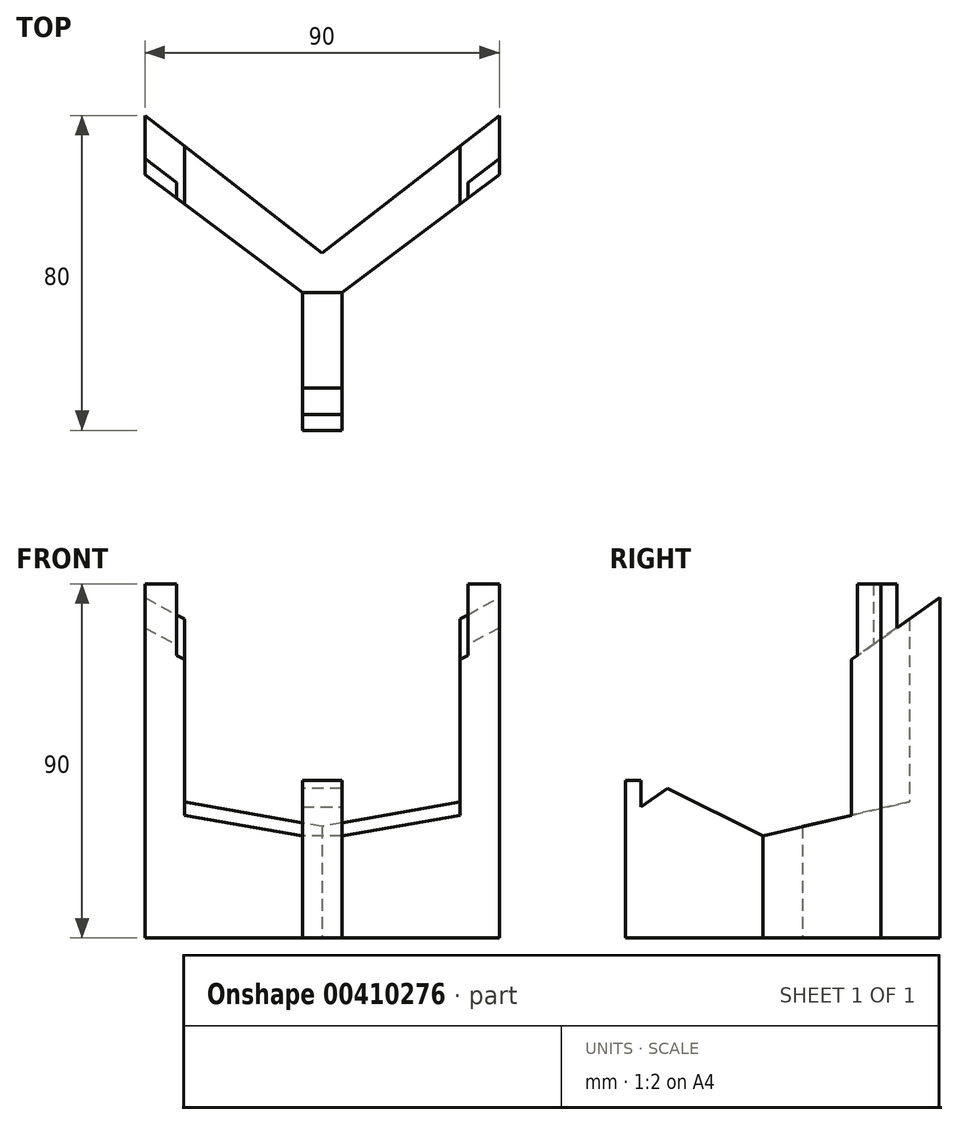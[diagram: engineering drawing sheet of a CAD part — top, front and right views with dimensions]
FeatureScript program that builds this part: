
annotation { "Feature Type Name" : "Feature", "Feature Type Description" : "" }
export const myFeature = defineFeature(function(context is Context, id is Id, definition is map)
    precondition{}
    {
        {
            var Q0;
            Q0=qCreatedBy(makeId("Top.planeOp"),FACE);
            var sketch = newSketch(context, id + "F0", { "sketchPlane" : qUnion([Q0])});
            skLineSegment(sketch, "E0", {"start": v(-5, -35) * mm, "end": v(5, -35) * mm});
            skLineSegment(sketch, "E1", {"start": v(5, -35) * mm, "end": v(5, 0) * mm});
            skLineSegment(sketch, "E2", {"start": v(5, 0) * mm, "end": v(45, 30) * mm});
            skLineSegment(sketch, "E3", {"start": v(45, 30) * mm, "end": v(45, 45) * mm});
            skLineSegment(sketch, "E4", {"start": v(45, 45) * mm, "end": v(0, 10) * mm});
            skLineSegment(sketch, "E5", {"start": v(0, 10) * mm, "end": v(-45, 45) * mm});
            skLineSegment(sketch, "E6", {"start": v(-45, 45) * mm, "end": v(-45, 30) * mm});
            skLineSegment(sketch, "E7", {"start": v(-5, -35) * mm, "end": v(-5, 0) * mm});
            skLineSegment(sketch, "E8", {"start": v(-5, 0) * mm, "end": v(-45, 30) * mm});
            skSolve(sketch);
        }
        {
            var Q0;
            Q0 = qSketchRegion(id + "F0", true);
            extrude(context, id + "F1", {"entities" : qUnion([Q0]), "depth" : 80 * mm});
        }
        {
            var Q0;
            Q0=makeQuery(id+"F1.opExtrude","SWEPT_FACE",FACE,{"disambiguationData":[OSD([sQuery(id+"F0.wireOp",EDGE,"E7")])]});
            var sketch = newSketch(context, id + "F2", { "sketchPlane" : qUnion([Q0])});
            skLineSegment(sketch, "E9", {"start": v(35, 80) * mm, "end": v(-50, 80) * mm});
            skLineSegment(sketch, "E10", {"start": v(-50, 80) * mm, "end": v(35, 20.48) * mm});
            skLineSegment(sketch, "E11", {"start": v(35, 20.48) * mm, "end": v(35, 80) * mm});
            skSolve(sketch);
        }
        {
            var Q0;
            Q0 = qSketchRegion(id + "F2", true);
            extrude(context, id + "F3", {"entities" : qUnion([Q0]), "operationType" : NewBodyOperationType.REMOVE, "endBound" : BoundingType.THROUGH_ALL, "oppositeDirection" : true, "depth" : 25 * mm, "hasSecondDirection" : true, "secondDirectionBound" : SecondDirectionBoundingType.THROUGH_ALL, "secondDirectionOppositeDirection" : false, "secondDirectionDepth" : 25 * mm});
        }
        {
            var Q0;
            Q0=makeQuery(id+"F1.opExtrude","SWEPT_FACE",FACE,{"disambiguationData":[OSD([sQuery(id+"F0.wireOp",EDGE,"E7")])]});
            var sketch = newSketch(context, id + "F4", { "sketchPlane" : qUnion([Q0])});
            skLineSegment(sketch, "E12", {"start": v(24.26, 28) * mm, "end": v(0, 16) * mm});
            skLineSegment(sketch, "E13", {"start": v(0, 16) * mm, "end": v(-51.74, 28) * mm});
            skLineSegment(sketch, "E14", {"start": v(-51.74, 28) * mm, "end": v(-51.74, 88) * mm});
            skLineSegment(sketch, "E15", {"start": v(-51.74, 88) * mm, "end": v(24.26, 88) * mm});
            skLineSegment(sketch, "E16", {"start": v(24.26, 88) * mm, "end": v(24.26, 28) * mm});
            skSolve(sketch);
        }
        {
            var Q0;
            Q0 = qSketchRegion(id + "F4", true);
            extrude(context, id + "F5", {"entities" : qUnion([Q0]), "operationType" : NewBodyOperationType.REMOVE, "oppositeDirection" : true, "depth" : 40 * mm, "hasSecondDirection" : true, "secondDirectionOppositeDirection" : false, "secondDirectionDepth" : 30 * mm});
        }
        {
            var Q0;
            Q0=makeQuery(id+"F1.opExtrude","CAP_FACE",FACE,{"disambiguationData":[OSD([sQuery(id+"F0.wireOp",EDGE,"E0"),sQuery(id+"F0.wireOp",EDGE,"E1"),sQuery(id+"F0.wireOp",EDGE,"E2"),sQuery(id+"F0.wireOp",EDGE,"E3"),sQuery(id+"F0.wireOp",EDGE,"E4"),sQuery(id+"F0.wireOp",EDGE,"E5"),sQuery(id+"F0.wireOp",EDGE,"E6"),sQuery(id+"F0.wireOp",EDGE,"E7"),sQuery(id+"F0.wireOp",EDGE,"E8")])],"isStart":true});
            var sketch = newSketch(context, id + "F6", { "sketchPlane" : qUnion([Q0])});
            skLineSegment(sketch, "E17.bottom", {"start": v(-5, 35) * mm, "end": v(5, 35) * mm});
            skLineSegment(sketch, "E17.top", {"start": v(-5, 31) * mm, "end": v(5, 31) * mm});
            skLineSegment(sketch, "E17.left", {"start": v(-5, 35) * mm, "end": v(-5, 31) * mm});
            skLineSegment(sketch, "E17.right", {"start": v(5, 35) * mm, "end": v(5, 31) * mm});
            skSolve(sketch);
        }
        {
            var Q0;
            Q0 = qSketchRegion(id + "F6", true);
            extrude(context, id + "F7", {"entities" : qUnion([Q0]), "operationType" : NewBodyOperationType.ADD, "oppositeDirection" : true, "depth" : 30 * mm});
        }
        {
            var Q0;
            Q0=makeQuery(id+"F1.opExtrude","CAP_FACE",FACE,{"disambiguationData":[OSD([sQuery(id+"F0.wireOp",EDGE,"E0"),sQuery(id+"F0.wireOp",EDGE,"E1"),sQuery(id+"F0.wireOp",EDGE,"E2"),sQuery(id+"F0.wireOp",EDGE,"E3"),sQuery(id+"F0.wireOp",EDGE,"E4"),sQuery(id+"F0.wireOp",EDGE,"E5"),sQuery(id+"F0.wireOp",EDGE,"E6"),sQuery(id+"F0.wireOp",EDGE,"E7"),sQuery(id+"F0.wireOp",EDGE,"E8")])],"isStart":true});
            var sketch = newSketch(context, id + "F8", { "sketchPlane" : qUnion([Q0])});
            skLineSegment(sketch, "E18", {"start": v(-45, -30) * mm, "end": v(-45, -34) * mm});
            skLineSegment(sketch, "E19", {"start": v(-45, -34) * mm, "end": v(-37, -28) * mm});
            skLineSegment(sketch, "E20", {"start": v(-37, -28) * mm, "end": v(-37, -24) * mm});
            skLineSegment(sketch, "E21", {"start": v(-37, -24) * mm, "end": v(-45, -30) * mm});
            skLineSegment(sketch, "E22", {"start": v(45, -30) * mm, "end": v(45, -34) * mm});
            skLineSegment(sketch, "E23", {"start": v(45, -34) * mm, "end": v(37, -28) * mm});
            skLineSegment(sketch, "E24", {"start": v(37, -28) * mm, "end": v(37, -24) * mm});
            skLineSegment(sketch, "E25", {"start": v(37, -24) * mm, "end": v(45, -30) * mm});
            skSolve(sketch);
        }
        {
            var Q0;
            Q0 = qSketchRegion(id + "F8", true);
            extrude(context, id + "F9", {"entities" : qUnion([Q0]), "operationType" : NewBodyOperationType.ADD, "oppositeDirection" : true, "depth" : 80 * mm});
        }
        {
            var Q0;
            Q0=makeQuery(id+"F1.opExtrude","CAP_FACE",FACE,{"disambiguationData":[OSD([sQuery(id+"F0.wireOp",EDGE,"E0"),sQuery(id+"F0.wireOp",EDGE,"E1"),sQuery(id+"F0.wireOp",EDGE,"E2"),sQuery(id+"F0.wireOp",EDGE,"E3"),sQuery(id+"F0.wireOp",EDGE,"E4"),sQuery(id+"F0.wireOp",EDGE,"E5"),sQuery(id+"F0.wireOp",EDGE,"E6"),sQuery(id+"F0.wireOp",EDGE,"E7"),sQuery(id+"F0.wireOp",EDGE,"E8")])],"isStart":true});
            var sketch = newSketch(context, id + "F10", { "sketchPlane" : qUnion([Q0])});
            skLineSegment(sketch, "E26", {"start": v(-5, 35) * mm, "end": v(5, 35) * mm});
            skLineSegment(sketch, "E27", {"start": v(5, 35) * mm, "end": v(5, 0) * mm});
            skLineSegment(sketch, "E28", {"start": v(5, 0) * mm, "end": v(45, -30) * mm});
            skLineSegment(sketch, "E29", {"start": v(45, -30) * mm, "end": v(45, -45) * mm});
            skLineSegment(sketch, "E30", {"start": v(45, -45) * mm, "end": v(0, -10) * mm});
            skLineSegment(sketch, "E31", {"start": v(0, -10) * mm, "end": v(-45, -45) * mm});
            skLineSegment(sketch, "E32", {"start": v(-45, -45) * mm, "end": v(-45, -30) * mm});
            skLineSegment(sketch, "E33", {"start": v(-45, -30) * mm, "end": v(-5, 0) * mm});
            skLineSegment(sketch, "E34", {"start": v(-5, 0) * mm, "end": v(-5, 35) * mm});
            skSolve(sketch);
        }
        {
            var Q0;
            Q0 = qSketchRegion(id + "F10", true);
            extrude(context, id + "F11", {"entities" : qUnion([Q0]), "operationType" : NewBodyOperationType.ADD, "depth" : 10 * mm});
        }
    });
